# Revit family: M_Valve_Balancing and Control_MEPcontent_Oventrop_Hydrocontrol VTR 10603
name_source: partatom
category: Pipe Accessories
revit_build: Autodesk Revit 2015 (Build: 20140223_1515(x64)
units: mm (PartAtom-declared; Revit-internal decimal feet)

## types (7) — shared parameters
Angle = 50.00°
Article Description = Bronze double regulating and commissioning valves
Article Type = Hydrocontrol VTR 10603
Black = Color RGB 35-35-35
Bronze = Color RGB 156-122-90
Content Supplier URL = www.mepcontent.eu
Custom = No
Description = Bronze double regulating and commissioning valves
EMCS Version = 2.0
ETIM Article Class = EC011463
Family Version = 10.14
Hb4 = 18 mm  [stored 0.0590551 ft]
Hb5 = 3 mm  [stored 0.00984252 ft]
Hlp1 = 22 mm  [stored 0.0721785 ft]
IFCExportAs = IfcValveType
IFCExportType = PRESSUREREDUCING
Lgt2 = 11 mm  [stored 0.0360892 ft]
MEPcontent Class = VALVE_BALANCING
Manufacturer = Oventrop
Manufacturer URL = http://www.oventrop.de
Model = Hydrocontrol VTR 10603
Pressure Drop = 0.0 Pa
Product Line = Oventrop
Revit Version = 2015
URL = www.stabiplan.com
r1 = 2 mm  [stored 0.00656168 ft]
r2 = 3 mm  [stored 0.00984252 ft]

## per-type parameters (varying)
| type | GTIN | H | Hb1 | Hb2 | Hb3 | Hb6 | L2 | Lenght | Lgt1 | Manufacturer Art. No. | NominalDiameter | OuterDiameter | Rad1 | Rad2 | Rad3 | Rad4 | Rad5 | SW | SW2 | Thread_Lenght |
| DN 40 | 4026755191677 | 140.3 mm | 153.78 mm | 50 mm | 5 mm  [stored 0.0164042 ft] | 67.186 mm | 11.658 mm | 120 mm | 21.1 mm  [stored 0.0692257 ft] | 1060312 | 38.100 mm | 48.3 mm | 27 mm | 25 mm  [stored 0.082021 ft] | 27.5 mm | 30 mm | 32 mm | 55 mm | 63.509 mm | 19.1 mm  [stored 0.062664 ft] |
| DN 50 | 4026755191684 | 150.3 mm | 166.834 mm | 50 mm | 15 mm  [stored 0.0492126 ft] | 76.557 mm | 15.155 mm | 150 mm | 27.7 mm | 1060316 | 50.800 mm | 60.3 mm | 34.5 mm | 32.5 mm | 35 mm | 37.5 mm | 39.5 mm | 70 mm | 80.829 mm | 25.7 mm |
| DN 32 | 4026755191660 | 138.3 mm | 151.169 mm | 50 mm | 1 mm  [stored 0.00328084 ft] | 63.806 mm | 10.492 mm | 110 mm | 21.1 mm  [stored 0.0692257 ft] | 1060310 | 31.750 mm | 42.4 mm | 24.5 mm  [stored 0.0803806 ft] | 22.5 mm | 25 mm  [stored 0.082021 ft] | 27.5 mm | 29.5 mm | 50 mm | 57.735 mm | 19.1 mm  [stored 0.062664 ft] |
| DN 25 | 4026755191653 | 121.3 mm | 128.977 mm | 25.24 mm | 13 mm | 48.991 mm | 8.394 mm | 97.5 mm | 18.8 mm  [stored 0.0616798 ft] | 1060308 | 25.400 mm | 33.7 mm | 20 mm  [stored 0.0656168 ft] | 18 mm  [stored 0.0590551 ft] | 20.5 mm  [stored 0.0672572 ft] | 23 mm  [stored 0.0754593 ft] | 25 mm  [stored 0.082021 ft] | 41 mm | 47.343 mm | 16.8 mm  [stored 0.0551181 ft] |
| DN 20 | 4026755191646 | 118.3 mm | 125.061 mm | 21.43 mm  [stored 0.0703084 ft] | 11 mm  [stored 0.0360892 ft] | 43.248 mm | 6.295 mm | 84 mm | 16.5 mm  [stored 0.0541339 ft] | 1060306 | 19.050 mm | 26.9 mm | 15.5 mm  [stored 0.050853 ft] | 13.5 mm  [stored 0.0442913 ft] | 16 mm  [stored 0.0524934 ft] | 18.5 mm  [stored 0.0606955 ft] | 20.5 mm  [stored 0.0672572 ft] | 32 mm | 36.95 mm | 14.5 mm  [stored 0.0475722 ft] |
| DN 15 | 4026755191639 | 116.3 mm | 122.45 mm | 17.62 mm  [stored 0.0578084 ft] | 15 mm  [stored 0.0492126 ft] | 45.337 mm | 5.129 mm | 80 mm | 15.2 mm | 1060304 | 12.700 mm | 21.3 mm  [stored 0.0698819 ft] | 13 mm | 11 mm  [stored 0.0360892 ft] | 13.5 mm  [stored 0.0442913 ft] | 16 mm  [stored 0.0524934 ft] | 18 mm  [stored 0.0590551 ft] | 27 mm | 31.177 mm | 13.2 mm  [stored 0.0433071 ft] |
| DN 10 | 4026755191622 | 116.3 mm | 122.45 mm | 15.715 mm  [stored 0.0515584 ft] | 15 mm  [stored 0.0492126 ft] | 43.771 mm | 5.129 mm | 73 mm | 12.1 mm | 1060303 | 9.525 mm | 17.2 mm | 13 mm | 11 mm  [stored 0.0360892 ft] | 13.5 mm  [stored 0.0442913 ft] | 16 mm  [stored 0.0524934 ft] | 18 mm  [stored 0.0590551 ft] | 27 mm | 31.177 mm | 10.1 mm |

note: [stored X ft] marks values corroborated as IEEE doubles in the binary element streams (Revit-internal decimal feet)

## geometry (parser evidence)
native form markers: Sweep x2
no freeform markers — native parametric forms only
